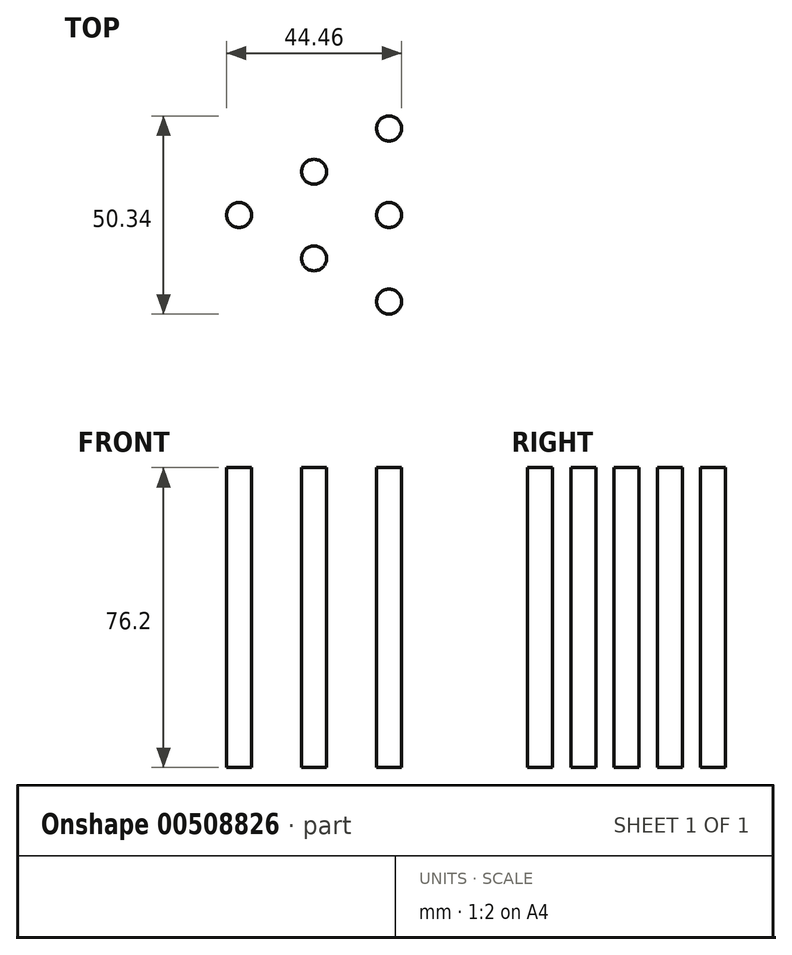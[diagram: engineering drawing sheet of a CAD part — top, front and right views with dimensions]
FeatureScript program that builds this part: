
annotation { "Feature Type Name" : "Feature", "Feature Type Description" : "" }
export const myFeature = defineFeature(function(context is Context, id is Id, definition is map)
    precondition{}
    {
        {
            var Q0;
            Q0=qCreatedBy(makeId("Right.planeOp"),FACE);
            var sketch = newSketch(context, id + "F0", { "sketchPlane" : qUnion([Q0])});
            skLineSegment(sketch, "E0", {"start": v(0, 0) * mm, "end": v(0, 179.6) * mm});
            skLineSegment(sketch, "E1", {"start": v(0, 179.6) * mm, "end": v(-169.33, -59.87) * mm});
            skLineSegment(sketch, "E2", {"start": v(-169.33, -59.87) * mm, "end": v(0, 0) * mm});
            skLineSegment(sketch, "E3", {"start": v(-169.33, -59.87) * mm, "end": v(84.67, -59.87) * mm, "construction": true});
            skLineSegment(sketch, "E4", {"start": v(0, 179.6) * mm, "end": v(84.67, -59.87) * mm, "construction": true});
            skLineSegment(sketch, "E5", {"start": v(0, 0) * mm, "end": v(84.67, -59.87) * mm, "construction": true});
            skLineSegment(sketch, "E6", {"start": v(0, 0) * mm, "end": v(0, -59.87) * mm, "construction": true});
            skCircle(sketch, "E7", {"center": v(-84.67, -59.87) * mm, "radius": 84.67 * mm, "construction": true});
            skCircle(sketch, "E8", {"center": v(0, -59.87) * mm, "radius": 84.67 * mm, "construction": true});
            skArc(sketch, "E9", {"start": v(-169.33, -59.87) * mm, "mid": v(-46.6, 32.96) * mm, "end": v(0, 179.6) * mm, "construction": true});
            skLineSegment(sketch, "E10", {"start": v(0, 179.6) * mm, "end": v(-254, 179.6) * mm, "construction": true});
            skLineSegment(sketch, "E11", {"start": v(-169.33, -59.87) * mm, "end": v(-254, 179.6) * mm, "construction": true});
            skSolve(sketch);
        }
        {
            var Q0;
            Q0=qCreatedBy(makeId("Right.planeOp"),FACE);
            var sketch = newSketch(context, id + "F1", { "sketchPlane" : qUnion([Q0])});
            skPoint(sketch, "E12.0", {"position": v(-254, 179.6) * mm});
            skPoint(sketch, "E13.0", {"position": v(-169.33, -59.87) * mm});
            skPoint(sketch, "E14.0", {"position": v(0, 0) * mm});
            skArc(sketch, "E15", {"start": v(-169.33, -59.87) * mm, "mid": v(-46.6, 32.96) * mm, "end": v(0, 179.6) * mm, "construction": true});
            skLineSegment(sketch, "E16", {"start": v(0, 179.6) * mm, "end": v(-254, 179.6) * mm, "construction": true});
            skLineSegment(sketch, "E17", {"start": v(-169.33, -59.87) * mm, "end": v(-254, 179.6) * mm, "construction": true});
            skCircle(sketch, "E18", {"center": v(-3.67, 0) * mm, "radius": 3.18 * mm, "construction": true});
            skCircle(sketch, "E19.1.0", {"center": v(1.83, -3.18) * mm, "radius": 3.18 * mm, "construction": true});
            skCircle(sketch, "E19.2.0", {"center": v(1.83, 3.18) * mm, "radius": 3.18 * mm, "construction": true});
            skLineSegment(sketch, "E20", {"start": v(1.83, 3.18) * mm, "end": v(1.83, -3.18) * mm, "construction": true});
            skLineSegment(sketch, "E21", {"start": v(-3.67, 0) * mm, "end": v(1.83, 0) * mm, "construction": true});
            skLineSegment(sketch, "E22", {"start": v(-3.67, 0) * mm, "end": v(-12.7, 0) * mm, "construction": true});
            skCircle(sketch, "E23", {"center": v(-12.7, 0) * mm, "radius": 3.18 * mm, "construction": true});
            skCircle(sketch, "E24.1.0", {"center": v(6.35, -11) * mm, "radius": 3.18 * mm, "construction": true});
            skCircle(sketch, "E24.2.0", {"center": v(6.35, 11) * mm, "radius": 3.18 * mm, "construction": true});
            skLineSegment(sketch, "E25", {"start": v(6.35, 11) * mm, "end": v(6.35, -11) * mm, "construction": true});
            skLineSegment(sketch, "E26", {"start": v(1.83, 0) * mm, "end": v(6.35, 0) * mm, "construction": true});
            skArc(sketch, "E27.0", {"start": v(-7.53, 135.81) * mm, "mid": v(-4.63, 157.62) * mm, "end": v(-3.67, 179.6) * mm});
            skLineSegment(sketch, "E28", {"start": v(-254, 179.6) * mm, "end": v(-32.17, 98.2) * mm, "construction": true});
            skLineSegment(sketch, "E29", {"start": v(-254, 179.6) * mm, "end": v(-7.53, 135.81) * mm, "construction": true});
            skLineSegment(sketch, "E30", {"start": v(-254, 179.6) * mm, "end": v(-49.83, 60.65) * mm, "construction": true});
            skLineSegment(sketch, "E31", {"start": v(-254, 179.6) * mm, "end": v(-73.8, 26.77) * mm, "construction": true});
            skArc(sketch, "E32", {"start": v(-175.24, -43.17) * mm, "mid": v(-61.07, 43.18) * mm, "end": v(-17.7, 179.6) * mm, "construction": true});
            skLineSegment(sketch, "E33", {"start": v(-73.8, 26.77) * mm, "end": v(-49.83, 60.65) * mm, "construction": true});
            skLineSegment(sketch, "E34", {"start": v(-49.83, 60.65) * mm, "end": v(-32.17, 98.2) * mm, "construction": true});
            skLineSegment(sketch, "E35", {"start": v(-32.17, 98.2) * mm, "end": v(-21.35, 138.27) * mm, "construction": true});
            skLineSegment(sketch, "E36", {"start": v(-21.35, 138.27) * mm, "end": v(-17.7, 179.6) * mm, "construction": true});
            skLineSegment(sketch, "E37", {"start": v(-254, 179.6) * mm, "end": v(-103.31, -2.4) * mm, "construction": true});
            skLineSegment(sketch, "E38", {"start": v(-73.8, 26.77) * mm, "end": v(-103.31, -2.4) * mm, "construction": true});
            skLineSegment(sketch, "E39", {"start": v(-254, 179.6) * mm, "end": v(-137.48, -25.96) * mm, "construction": true});
            skLineSegment(sketch, "E40", {"start": v(-175.24, -43.17) * mm, "end": v(-137.48, -25.96) * mm, "construction": true});
            skLineSegment(sketch, "E41", {"start": v(-103.31, -2.4) * mm, "end": v(-137.48, -25.96) * mm, "construction": true});
            skSolve(sketch);
        }
        {
            var Q0;
            Q0=qCreatedBy(makeId("Right.planeOp"),FACE);
            var sketch = newSketch(context, id + "F2", { "sketchPlane" : qUnion([Q0])});
            skPoint(sketch, "E42.0", {"position": v(-3.67, 179.6) * mm});
            skPoint(sketch, "E42.1", {"position": v(-7.53, 135.81) * mm});
            skPoint(sketch, "E42.2", {"position": v(-254, 179.6) * mm});
            skPoint(sketch, "E42.3", {"position": v(0, 0) * mm});
            skPoint(sketch, "E42.4", {"position": v(-12.7, 0) * mm});
            skArc(sketch, "E43", {"start": v(-7.53, 135.81) * mm, "mid": v(-4.63, 157.62) * mm, "end": v(-3.67, 179.6) * mm});
            skLineSegment(sketch, "E44", {"start": v(-7.53, 135.81) * mm, "end": v(-8.84, 128.42) * mm});
            skLineSegment(sketch, "E45", {"start": v(-8.18, 132.12) * mm, "end": v(-8.18, 84.63) * mm, "construction": true});
            skArc(sketch, "E46.1.0", {"start": v(-8.84, 128.42) * mm, "mid": v(-11.73, 106.61) * mm, "end": v(-12.7, 84.63) * mm});
            skPoint(sketch, "E46.center", {"position": v(-8.18, 132.12) * mm});
            skSolve(sketch);
        }
        {
            var Q0;
            Q0=qCreatedBy(makeId("Right.planeOp"),FACE);
            var sketch = newSketch(context, id + "F3", { "sketchPlane" : qUnion([Q0])});
            skPoint(sketch, "E47.0", {"position": v(0, 0) * mm});
            skPoint(sketch, "E48.0", {"position": v(-3.67, 179.6) * mm});
            skPoint(sketch, "E48.1", {"position": v(-7.53, 135.81) * mm});
            skPoint(sketch, "E48.2", {"position": v(-254, 179.6) * mm});
            skArc(sketch, "E49", {"start": v(-7.53, 135.81) * mm, "mid": v(-4.63, 157.62) * mm, "end": v(-3.67, 179.6) * mm});
            skLineSegment(sketch, "E50", {"start": v(-7.53, 135.81) * mm, "end": v(-21.54, 56.95) * mm});
            skLineSegment(sketch, "E51", {"start": v(-14.53, 96.38) * mm, "end": v(-14.53, 13.15) * mm, "construction": true});
            skArc(sketch, "E52.1.0", {"start": v(-21.54, 56.95) * mm, "mid": v(-24.43, 35.14) * mm, "end": v(-25.4, 13.15) * mm});
            skPoint(sketch, "E52.center", {"position": v(-14.53, 96.38) * mm});
            skLineSegment(sketch, "E53", {"start": v(0, 0) * mm, "end": v(-25.4, 0) * mm, "construction": true});
            skSolve(sketch);
        }
        {
            var Q0;
            Q0=sQuery(id+"F0.wireOp",VERTEX,"E8.center");
            var Q1;
            Q1=qCreatedBy(makeId("Top.planeOp"),FACE);
            cPlane(context, id + "F4", {"entities" : qUnion([Q0, Q1]), "cplaneType" : CPlaneType.PLANE_POINT, "offset" : 25.4 * mm, "width" : 152.4 * mm, "height" : 152.4 * mm});
        }
        {
            var Q0;
            Q0=qCreatedBy(id+"F4.planeOp",FACE);
            var sketch = newSketch(context, id + "F5", { "sketchPlane" : qUnion([Q0])});
            skCircle(sketch, "E54.cCircle", {"center": v(0, 0) * mm, "radius": 169.33 * mm, "construction": true});
            skLineSegment(sketch, "E54.0", {"start": v(0, -169.33) * mm, "end": v(-146.65, 84.67) * mm, "construction": true});
            skLineSegment(sketch, "E54.1", {"start": v(-146.65, 84.67) * mm, "end": v(146.65, 84.67) * mm, "construction": true});
            skLineSegment(sketch, "E54.2", {"start": v(146.65, 84.67) * mm, "end": v(0, -169.33) * mm, "construction": true});
            skSolve(sketch);
        }
        {
            var Q0;
            Q0=sQuery(id+"F0.wireOp",VERTEX,"E6.start");
            var Q1;
            Q1=sQuery(id+"F5.wireOp",VERTEX,"E54.1.start");
            var Q2;
            Q2=sQuery(id+"F5.wireOp",VERTEX,"E54.2.start");
            cPlane(context, id + "F6", {"entities" : qUnion([Q0, Q1, Q2]), "cplaneType" : CPlaneType.THREE_POINT, "offset" : 25.4 * mm, "width" : 152.4 * mm, "height" : 152.4 * mm});
        }
        {
            var Q0;
            Q0=qCreatedBy(id+"F6.planeOp",FACE);
            var sketch = newSketch(context, id + "F7", { "sketchPlane" : qUnion([Q0])});
            skLineSegment(sketch, "E55", {"start": v(-146.65, 103.7) * mm, "end": v(0, 0) * mm});
            skLineSegment(sketch, "E56", {"start": v(0, 0) * mm, "end": v(146.65, 103.7) * mm});
            skLineSegment(sketch, "E57", {"start": v(146.65, 103.7) * mm, "end": v(-146.65, 103.7) * mm});
            skLineSegment(sketch, "E58", {"start": v(0, 103.7) * mm, "end": v(0, 0) * mm});
            skSolve(sketch);
        }
        {
            var Q0;
            Q0=sQuery(id+"F7.wireOp",VERTEX,"E57.end");
            var Q1;
            Q1=sQuery(id+"F7.wireOp",VERTEX,"E57.start");
            var Q2;
            Q2=sQuery(id+"F0.wireOp",VERTEX,"E4.start");
            cPlane(context, id + "F8", {"entities" : qUnion([Q0, Q1, Q2]), "cplaneType" : CPlaneType.THREE_POINT, "offset" : 25.4 * mm, "width" : 152.4 * mm, "height" : 152.4 * mm});
        }
        {
            var Q0;
            Q0=sQuery(id+"F1.wireOp",VERTEX,"E27.0.end");
            var Q1;
            Q1=qCreatedBy(makeId("Top.planeOp"),FACE);
            cPlane(context, id + "F9", {"entities" : qUnion([Q0, Q1]), "cplaneType" : CPlaneType.PLANE_POINT, "offset" : 25.4 * mm, "width" : 152.4 * mm, "height" : 152.4 * mm});
        }
        {
            var Q0;
            Q0=qCreatedBy(id+"F9.planeOp",FACE);
            var sketch = newSketch(context, id + "F10", { "sketchPlane" : qUnion([Q0])});
            skPoint(sketch, "E59.0", {"position": v(0, -3.67) * mm});
            skCircle(sketch, "E60", {"center": v(0, -3.67) * mm, "radius": 3.18 * mm});
            skSolve(sketch);
        }
        {
            var Q0;
            Q0=qCreatedBy(makeId("Top.planeOp"),FACE);
            var sketch = newSketch(context, id + "F11", { "sketchPlane" : qUnion([Q0])});
            skCircle(sketch, "E61", {"center": v(-6.35, -11) * mm, "radius": 3.18 * mm});
            skCircle(sketch, "E62", {"center": v(-25.4, 0) * mm, "radius": 3.18 * mm});
            skCircle(sketch, "E63.1.0", {"center": v(12.7, 0) * mm, "radius": 3.18 * mm});
            skCircle(sketch, "E63.2.0", {"center": v(-6.35, 11) * mm, "radius": 3.18 * mm});
            skPoint(sketch, "E63.center", {"position": v(0, 0) * mm});
            skCircle(sketch, "E64.1.0", {"center": v(12.7, -22) * mm, "radius": 3.18 * mm});
            skCircle(sketch, "E64.2.0", {"center": v(12.7, 22) * mm, "radius": 3.18 * mm});
            skLineSegment(sketch, "E65", {"start": v(0, 0) * mm, "end": v(12.7, 0) * mm});
            skLineSegment(sketch, "E66", {"start": v(0, 0) * mm, "end": v(-25.4, 0) * mm});
            skSolve(sketch);
        }
        {
            var Q0;
            Q0=makeQuery(id+"F11.imprint","IMPRINT",FACE,{"disambiguationData":[TD([[makeQuery(id+"F11.imprint","IMPRINT",EDGE,{"derivedFrom":sQuery(id+"F11.wireOp",EDGE,"E64.1.0")}),1.0]])]});
            var Q1;
            Q1=makeQuery(id+"F11.imprint","IMPRINT",FACE,{"disambiguationData":[TD([[makeQuery(id+"F11.imprint","IMPRINT",EDGE,{"derivedFrom":sQuery(id+"F11.wireOp",EDGE,"E63.2.0")}),1.0]])]});
            var Q2;
            Q2=makeQuery(id+"F11.imprint","IMPRINT",FACE,{"disambiguationData":[TD([[makeQuery(id+"F11.imprint","IMPRINT",EDGE,{"derivedFrom":sQuery(id+"F11.wireOp",EDGE,"E62")}),1.0]])]});
            var Q3;
            Q3=makeQuery(id+"F11.imprint","IMPRINT",FACE,{"disambiguationData":[TD([[makeQuery(id+"F11.imprint","IMPRINT",EDGE,{"derivedFrom":sQuery(id+"F11.wireOp",EDGE,"E63.1.0")}),1.0]])]});
            var Q4;
            Q4=makeQuery(id+"F11.imprint","IMPRINT",FACE,{"disambiguationData":[TD([[makeQuery(id+"F11.imprint","IMPRINT",EDGE,{"derivedFrom":sQuery(id+"F11.wireOp",EDGE,"E61")}),1.0]])]});
            var Q5;
            Q5=makeQuery(id+"F11.imprint","IMPRINT",FACE,{"disambiguationData":[TD([[makeQuery(id+"F11.imprint","IMPRINT",EDGE,{"derivedFrom":sQuery(id+"F11.wireOp",EDGE,"E64.2.0")}),1.0]])]});
            extrude(context, id + "F12", {"entities" : qUnion([Q0, Q1, Q2, Q3, Q4, Q5]), "depth" : 76.2 * mm, "offsetDistance" : 25.4 * mm, "symmetric" : true});
        }
    });
